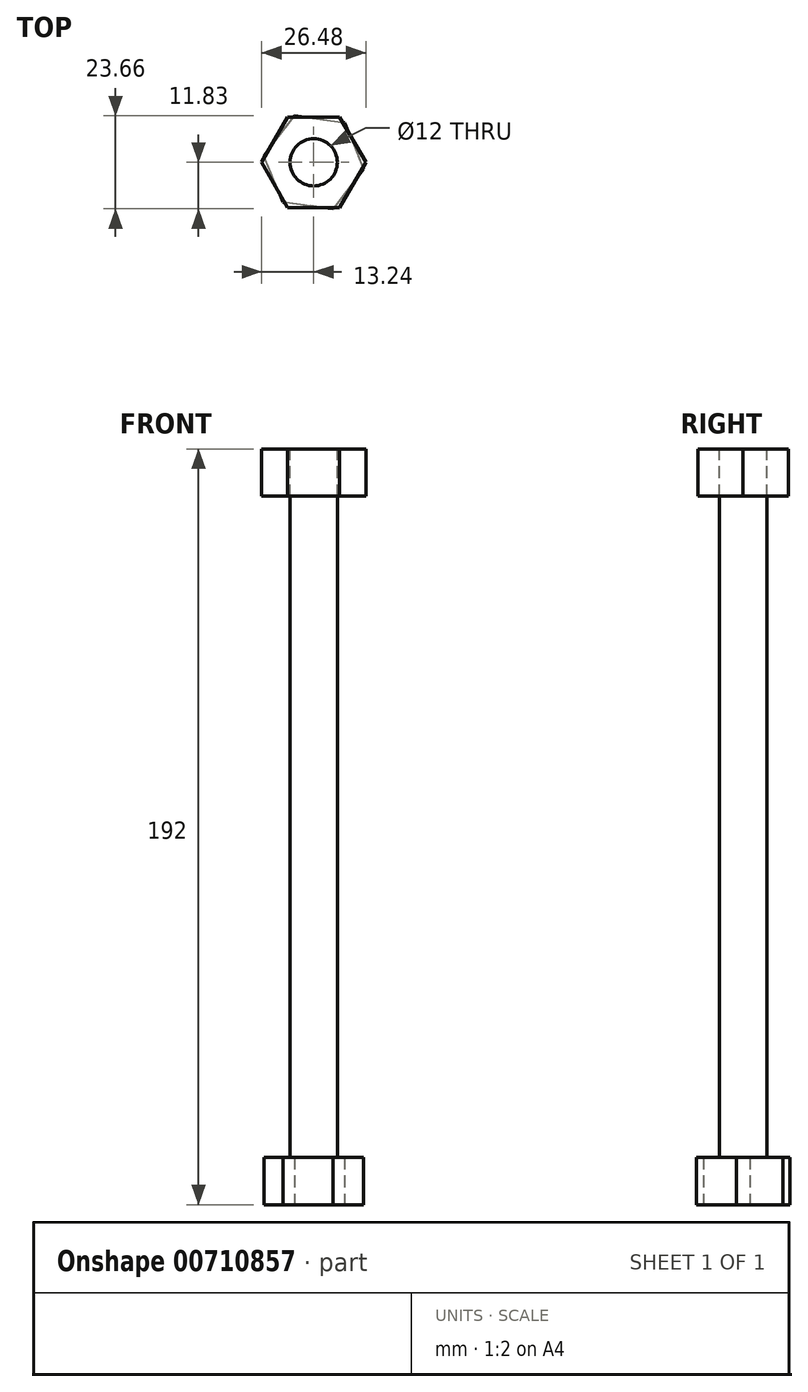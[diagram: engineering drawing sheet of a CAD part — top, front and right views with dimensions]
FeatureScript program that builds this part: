
annotation { "Feature Type Name" : "Feature", "Feature Type Description" : "" }
export const myFeature = defineFeature(function(context is Context, id is Id, definition is map)
    precondition{}
    {
        {
            var Q0;
            Q0=qCreatedBy(makeId("Top.planeOp"),FACE);
            var sketch = newSketch(context, id + "F0", { "sketchPlane" : qUnion([Q0])});
            skCircle(sketch, "E0", {"center": v(0, 0) * mm, "radius": 6 * mm});
            skCircle(sketch, "E1.cCircle", {"center": v(0, 0) * mm, "radius": 11.08 * mm, "construction": true});
            skLineSegment(sketch, "E1.0", {"start": v(-12.68, 1.69) * mm, "end": v(-4.88, 11.83) * mm});
            skLineSegment(sketch, "E1.1", {"start": v(-4.88, 11.83) * mm, "end": v(7.8, 10.14) * mm});
            skLineSegment(sketch, "E1.2", {"start": v(7.8, 10.14) * mm, "end": v(12.68, -1.69) * mm});
            skLineSegment(sketch, "E1.3", {"start": v(12.68, -1.69) * mm, "end": v(4.88, -11.83) * mm});
            skLineSegment(sketch, "E1.4", {"start": v(4.88, -11.83) * mm, "end": v(-7.8, -10.14) * mm});
            skLineSegment(sketch, "E1.5", {"start": v(-7.8, -10.14) * mm, "end": v(-12.68, 1.69) * mm});
            skPoint(sketch, "E1.0.midPoint", {"position": v(-8.78, 6.76) * mm});
            skSolve(sketch);
        }
        {
            var Q0;
            Q0=makeQuery(id+"F0.imprint","IMPRINT",FACE,{"disambiguationData":[TD([[makeQuery(id+"F0.imprint","IMPRINT",EDGE,{"derivedFrom":sQuery(id+"F0.wireOp",EDGE,"E0")}),1.0]])]});
            extrude(context, id + "F1", {"entities" : qUnion([Q0]), "depth" : 192 * mm, "offsetDistance" : 25 * mm});
        }
        {
            var Q0;
            Q0=qSketchRegion(id+"F0",true);
            extrude(context, id + "F2", {"entities" : qUnion([Q0]), "operationType" : NewBodyOperationType.ADD, "depth" : 12 * mm, "offsetDistance" : 25 * mm});
        }
        {
            var Q0;
            Q0=makeQuery(id+"F1.opExtrude","CAP_FACE",FACE,{"disambiguationData":[OSD([sQuery(id+"F0.wireOp",EDGE,"E0")])],"isStart":false});
            var sketch = newSketch(context, id + "F3", { "sketchPlane" : qUnion([Q0])});
            skCircle(sketch, "E2.cCircle", {"center": v(0, 0) * mm, "radius": 11.47 * mm, "construction": true});
            skLineSegment(sketch, "E2.0", {"start": v(6.62, -11.47) * mm, "end": v(-6.62, -11.47) * mm});
            skLineSegment(sketch, "E2.1", {"start": v(-6.62, -11.47) * mm, "end": v(-13.24, 0) * mm});
            skLineSegment(sketch, "E2.2", {"start": v(-13.24, 0) * mm, "end": v(-6.62, 11.47) * mm});
            skLineSegment(sketch, "E2.3", {"start": v(-6.62, 11.47) * mm, "end": v(6.62, 11.47) * mm});
            skLineSegment(sketch, "E2.4", {"start": v(6.62, 11.47) * mm, "end": v(13.24, 0) * mm});
            skLineSegment(sketch, "E2.5", {"start": v(13.24, 0) * mm, "end": v(6.62, -11.47) * mm});
            skPoint(sketch, "E2.0.midPoint", {"position": v(0, -11.47) * mm});
            skSolve(sketch);
        }
        {
            var Q0;
            Q0=makeQuery(id+"F3.imprint","IMPRINT",FACE,{"disambiguationData":[TD([[makeQuery(id+"F3.imprint","IMPRINT",EDGE,{"derivedFrom":sQuery(id+"F3.wireOp",EDGE,"E2.0")}),-1.0]])]});
            extrude(context, id + "F4", {"entities" : qUnion([Q0]), "oppositeDirection" : true, "depth" : 12 * mm, "offsetDistance" : 25 * mm});
        }
    });
